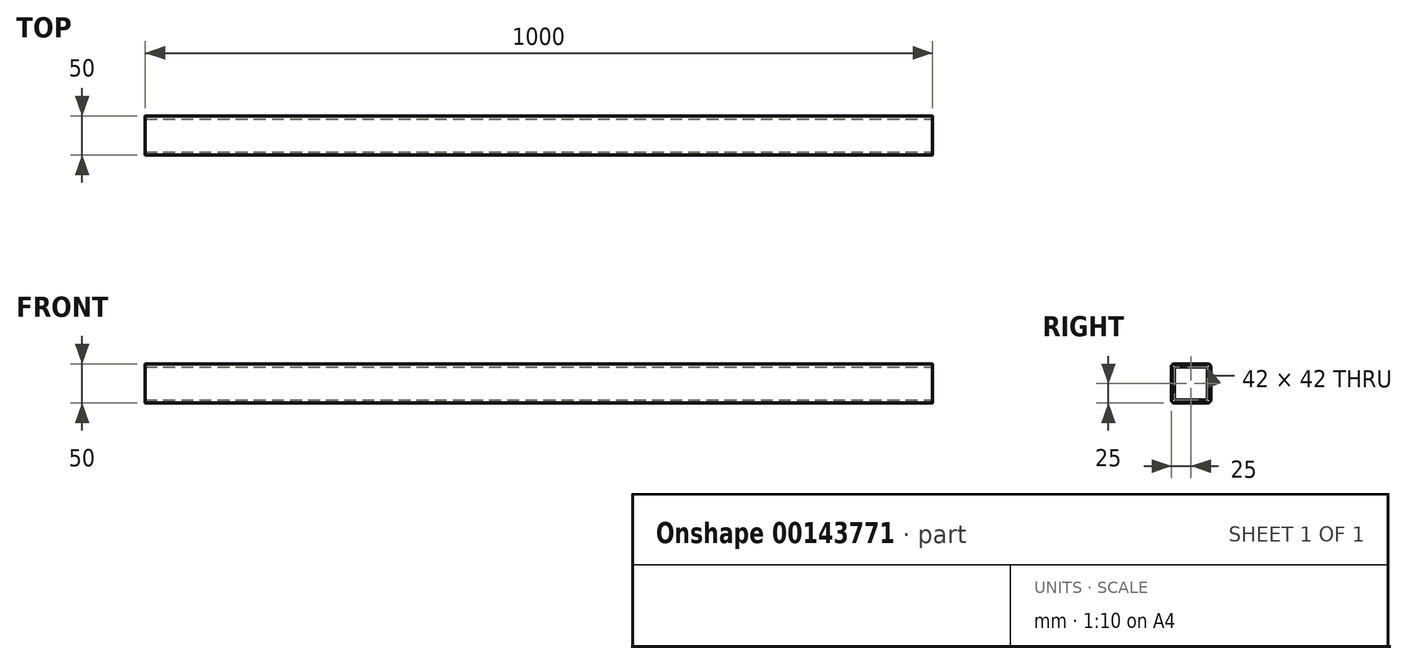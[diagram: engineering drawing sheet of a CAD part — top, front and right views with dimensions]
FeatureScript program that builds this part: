
annotation { "Feature Type Name" : "Feature", "Feature Type Description" : "" }
export const myFeature = defineFeature(function(context is Context, id is Id, definition is map)
    precondition{}
    {
        {
            var Q0;
            Q0=qCreatedBy(makeId("Right.planeOp"),FACE);
            var sketch = newSketch(context, id + "F0", { "sketchPlane" : qUnion([Q0])});
            skLineSegment(sketch, "E0.bottom", {"start": v(-21, 25) * mm, "end": v(21, 25) * mm});
            skLineSegment(sketch, "E0.top", {"start": v(-21, -25) * mm, "end": v(21, -25) * mm});
            skLineSegment(sketch, "E0.left", {"start": v(-25, 21) * mm, "end": v(-25, -21) * mm});
            skLineSegment(sketch, "E0.right", {"start": v(25, 21) * mm, "end": v(25, -21) * mm});
            skPoint(sketch, "E1.visualSharp", {"position": v(-25, 25) * mm});
            skArc(sketch, "E1.filletArc", {"start": v(-21, 25) * mm, "mid": v(-23.83, 23.83) * mm, "end": v(-25, 21) * mm});
            skPoint(sketch, "E2.visualSharp", {"position": v(-25, -25) * mm});
            skArc(sketch, "E2.filletArc", {"start": v(-25, -21) * mm, "mid": v(-23.83, -23.83) * mm, "end": v(-21, -25) * mm});
            skPoint(sketch, "E3.visualSharp", {"position": v(25, -25) * mm});
            skArc(sketch, "E3.filletArc", {"start": v(21, -25) * mm, "mid": v(23.83, -23.83) * mm, "end": v(25, -21) * mm});
            skPoint(sketch, "E4.visualSharp", {"position": v(25, 25) * mm});
            skArc(sketch, "E4.filletArc", {"start": v(25, 21) * mm, "mid": v(23.83, 23.83) * mm, "end": v(21, 25) * mm});
            skLineSegment(sketch, "E5.0", {"start": v(21, 21) * mm, "end": v(21, -21) * mm});
            skLineSegment(sketch, "E5.1", {"start": v(-21, 21) * mm, "end": v(21, 21) * mm});
            skLineSegment(sketch, "E5.2", {"start": v(-21, 21) * mm, "end": v(-21, -21) * mm});
            skLineSegment(sketch, "E5.3", {"start": v(-21, -21) * mm, "end": v(21, -21) * mm});
            skSolve(sketch);
        }
        {
            var Q0;
            Q0=makeQuery(id+"F0.imprint","IMPRINT",FACE,{"disambiguationData":[TD([[makeQuery(id+"F0.imprint","IMPRINT",EDGE,{"derivedFrom":sQuery(id+"F0.wireOp",EDGE,"E0.bottom")}),-1.0]])]});
            extrude(context, id + "F1", {"entities" : qUnion([Q0]), "endBound" : BoundingType.SYMMETRIC, "oppositeDirection" : true, "depth" : 1000 * mm});
        }
    });
